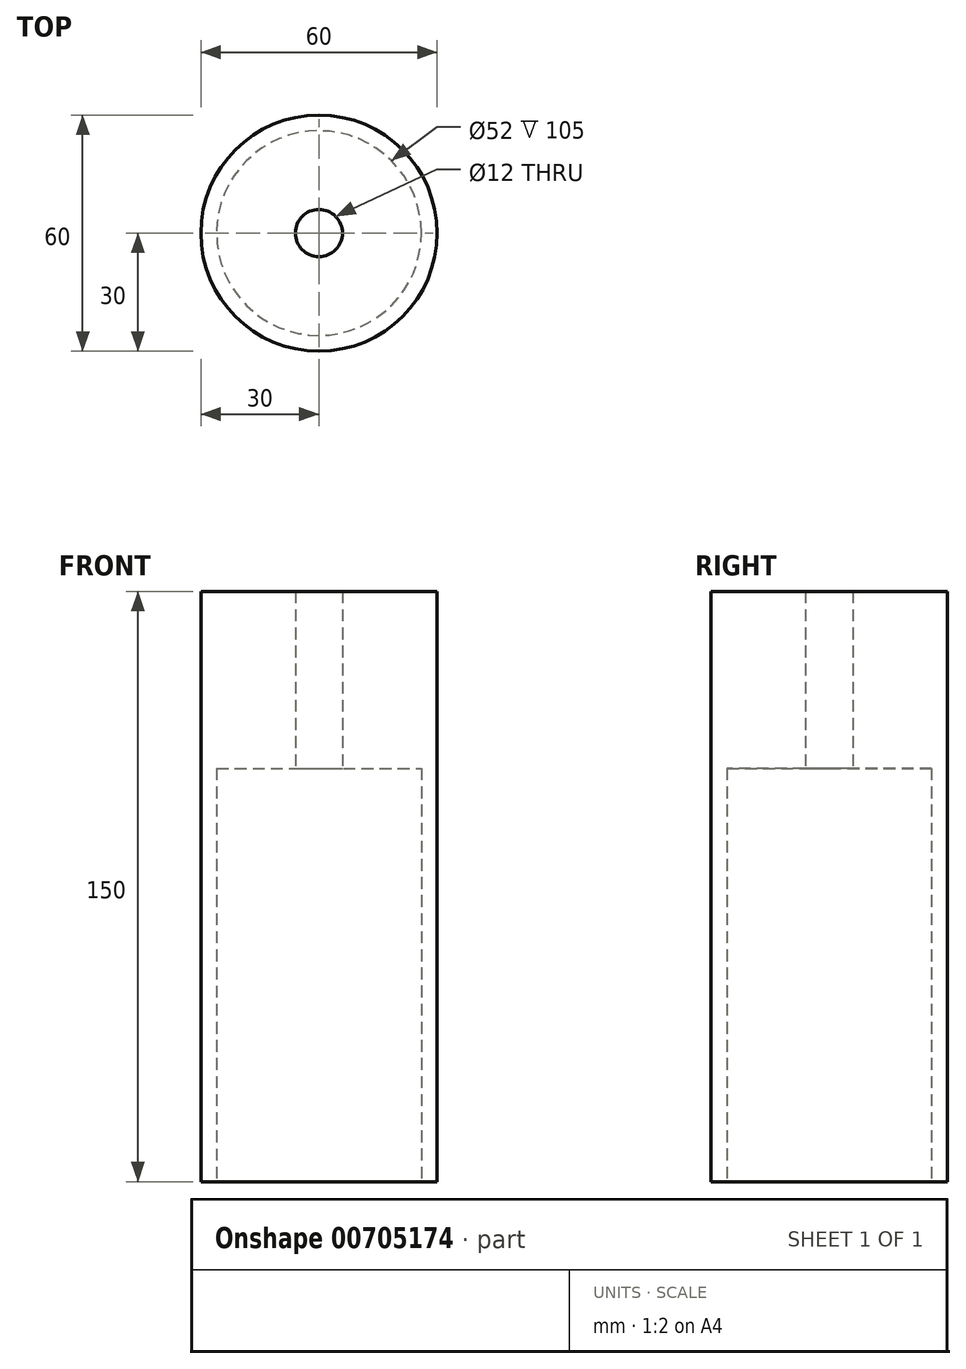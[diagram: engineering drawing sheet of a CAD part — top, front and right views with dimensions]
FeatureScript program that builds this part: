
annotation { "Feature Type Name" : "Feature", "Feature Type Description" : "" }
export const myFeature = defineFeature(function(context is Context, id is Id, definition is map)
    precondition{}
    {
        {
            var Q0;
            Q0=qCreatedBy(makeId("Front.planeOp"),FACE);
            var sketch = newSketch(context, id + "F0", { "sketchPlane" : qUnion([Q0])});
            skLineSegment(sketch, "E0.bottom", {"start": v(-26, 0) * mm, "end": v(-30, 0) * mm});
            skLineSegment(sketch, "E0.top", {"start": v(0, 150) * mm, "end": v(0, 150) * mm});
            skLineSegment(sketch, "E0.left", {"start": v(0, 105) * mm, "end": v(0, 150) * mm, "construction": true});
            skLineSegment(sketch, "E0.right", {"start": v(-30, 0) * mm, "end": v(-30, 150) * mm});
            skPoint(sketch, "E1.visualSharp", {"position": v(-30, 150) * mm});
            skLineSegment(sketch, "E2", {"start": v(-30, 150) * mm, "end": v(-6, 150) * mm});
            skLineSegment(sketch, "E3.top", {"start": v(-6, 105) * mm, "end": v(-26, 105) * mm});
            skLineSegment(sketch, "E3.right", {"start": v(-26, 0) * mm, "end": v(-26, 105) * mm});
            skLineSegment(sketch, "E4", {"start": v(-6, 150) * mm, "end": v(-6, 105) * mm});
            skSolve(sketch);
        }
        {
            var Q0;
            Q0=qSketchRegion(id+"F0",true);
            var Q1;
            Q1=sQuery(id+"F0.wireOp",EDGE,"E0.left");
            revolve(context, id + "F1", {"entities" : qUnion([Q0]), "axis" : qUnion([Q1]), "revolveType" : RevolveType.FULL});
        }
    });
